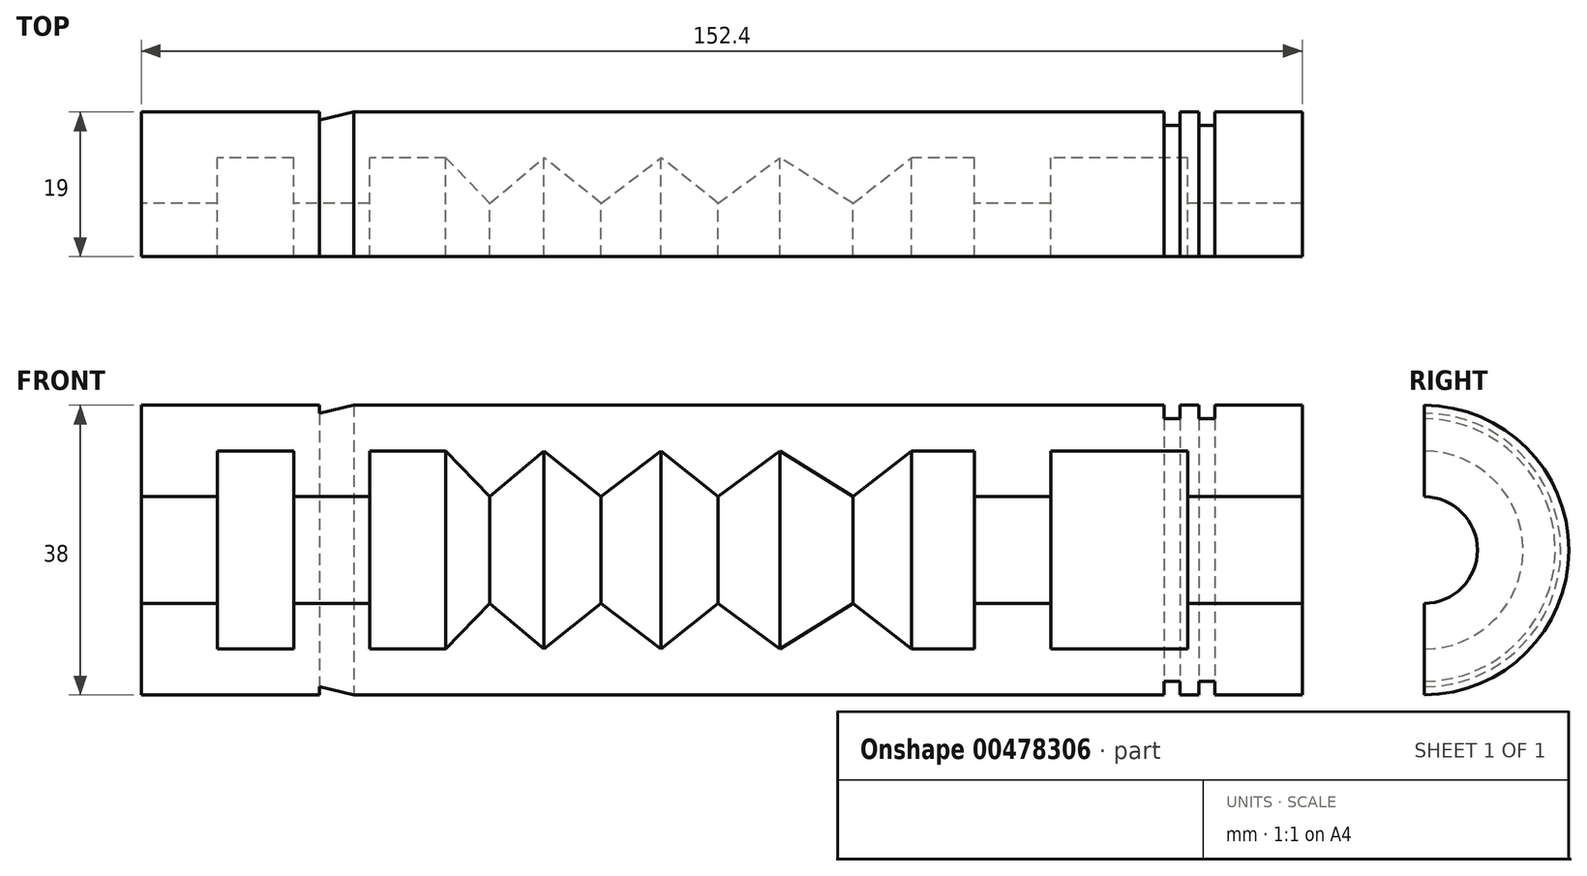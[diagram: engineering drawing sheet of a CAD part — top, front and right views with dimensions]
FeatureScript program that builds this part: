
annotation { "Feature Type Name" : "Feature", "Feature Type Description" : "" }
export const myFeature = defineFeature(function(context is Context, id is Id, definition is map)
    precondition{}
    {
        {
            var Q0;
            Q0=qCreatedBy(makeId("Front.planeOp"),FACE);
            var sketch = newSketch(context, id + "F0", { "sketchPlane" : qUnion([Q0])});
            skLineSegment(sketch, "E0", {"start": v(0, 0) * mm, "end": v(-11.45, 0) * mm});
            skLineSegment(sketch, "E1", {"start": v(-152.4, 12) * mm, "end": v(-152.4, 0) * mm});
            skLineSegment(sketch, "E2", {"start": v(-152.4, 12) * mm, "end": v(-142.4, 12) * mm});
            skLineSegment(sketch, "E3", {"start": v(-142.4, 12) * mm, "end": v(-142.4, 6) * mm});
            skLineSegment(sketch, "E4", {"start": v(-142.4, 6) * mm, "end": v(-132.4, 6) * mm});
            skLineSegment(sketch, "E5", {"start": v(-132.4, 6) * mm, "end": v(-132.4, 12) * mm});
            skLineSegment(sketch, "E6", {"start": v(-132.4, 12) * mm, "end": v(-122.4, 12) * mm});
            skLineSegment(sketch, "E7", {"start": v(-122.4, 12) * mm, "end": v(-122.4, 6) * mm});
            skLineSegment(sketch, "E8", {"start": v(-122.4, 6) * mm, "end": v(-112.4, 6) * mm});
            skLineSegment(sketch, "E9", {"start": v(-112.4, 6) * mm, "end": v(-106.63, 12) * mm});
            skLineSegment(sketch, "E10", {"start": v(-106.63, 12) * mm, "end": v(-99.52, 6) * mm});
            skLineSegment(sketch, "E11", {"start": v(-99.52, 6) * mm, "end": v(-92.03, 12) * mm});
            skLineSegment(sketch, "E12", {"start": v(-92.03, 12) * mm, "end": v(-84.15, 6) * mm});
            skLineSegment(sketch, "E13", {"start": v(-84.15, 6) * mm, "end": v(-76.65, 12) * mm});
            skLineSegment(sketch, "E14", {"start": v(-76.65, 12) * mm, "end": v(-68.58, 6) * mm});
            skLineSegment(sketch, "E15", {"start": v(-68.58, 6) * mm, "end": v(-58.97, 12) * mm});
            skLineSegment(sketch, "E16", {"start": v(-58.97, 12) * mm, "end": v(-51.28, 6) * mm});
            skLineSegment(sketch, "E17", {"start": v(-51.28, 6) * mm, "end": v(-43.02, 6) * mm});
            skLineSegment(sketch, "E18", {"start": v(-43.02, 6) * mm, "end": v(-43.02, 12) * mm});
            skLineSegment(sketch, "E19", {"start": v(-43.02, 12) * mm, "end": v(-33.02, 12) * mm});
            skLineSegment(sketch, "E20", {"start": v(-33.02, 12) * mm, "end": v(-33.02, 6) * mm});
            skLineSegment(sketch, "E21", {"start": v(-33.02, 6) * mm, "end": v(-15, 6) * mm});
            skLineSegment(sketch, "E22", {"start": v(-15, 6) * mm, "end": v(-15, 12) * mm});
            skLineSegment(sketch, "E23", {"start": v(-15, 12) * mm, "end": v(0, 12) * mm});
            skLineSegment(sketch, "E24", {"start": v(0, 12) * mm, "end": v(0, 0) * mm});
            skLineSegment(sketch, "E25", {"start": v(-181.38, 19) * mm, "end": v(36.9, 19) * mm});
            skLineSegment(sketch, "E26", {"start": v(-13.55, 0) * mm, "end": v(-13.55, 1.77) * mm});
            skLineSegment(sketch, "E27", {"start": v(-13.55, 1.77) * mm, "end": v(-11.45, 1.77) * mm});
            skLineSegment(sketch, "E28", {"start": v(-11.45, 1.77) * mm, "end": v(-11.45, 0) * mm});
            skLineSegment(sketch, "E29", {"start": v(-13.55, 0) * mm, "end": v(-16.02, 0) * mm});
            skLineSegment(sketch, "E30", {"start": v(-16.02, 0) * mm, "end": v(-16.02, 1.77) * mm});
            skLineSegment(sketch, "E31", {"start": v(-16.02, 1.77) * mm, "end": v(-18.12, 1.77) * mm});
            skLineSegment(sketch, "E32", {"start": v(-18.12, 1.77) * mm, "end": v(-18.12, 0) * mm});
            skLineSegment(sketch, "E33.trimOffspring", {"start": v(-18.12, 0) * mm, "end": v(-124.51, 0) * mm});
            skLineSegment(sketch, "E34", {"start": v(-129.02, 0) * mm, "end": v(-129.02, 1.07) * mm});
            skLineSegment(sketch, "E35", {"start": v(-129.02, 1.07) * mm, "end": v(-124.51, 0) * mm});
            skLineSegment(sketch, "E36.trimOffspring", {"start": v(-129.02, 0) * mm, "end": v(-152.4, 0) * mm});
            skSolve(sketch);
        }
        {
            var Q0;
            Q0=makeQuery(id+"F0.imprint","IMPRINT",FACE,{"disambiguationData":[TD([[makeQuery(id+"F0.imprint","IMPRINT",EDGE,{"derivedFrom":sQuery(id+"F0.wireOp",EDGE,"E0")}),-1.0]])]});
            var Q1;
            Q1=sQuery(id+"F0.wireOp",EDGE,"E25");
            revolve(context, id + "F1", {"entities" : qUnion([Q0]), "axis" : qUnion([Q1]), "revolveType" : RevolveType.ONE_DIRECTION, "angle" : 180 * degree});
        }
    });
